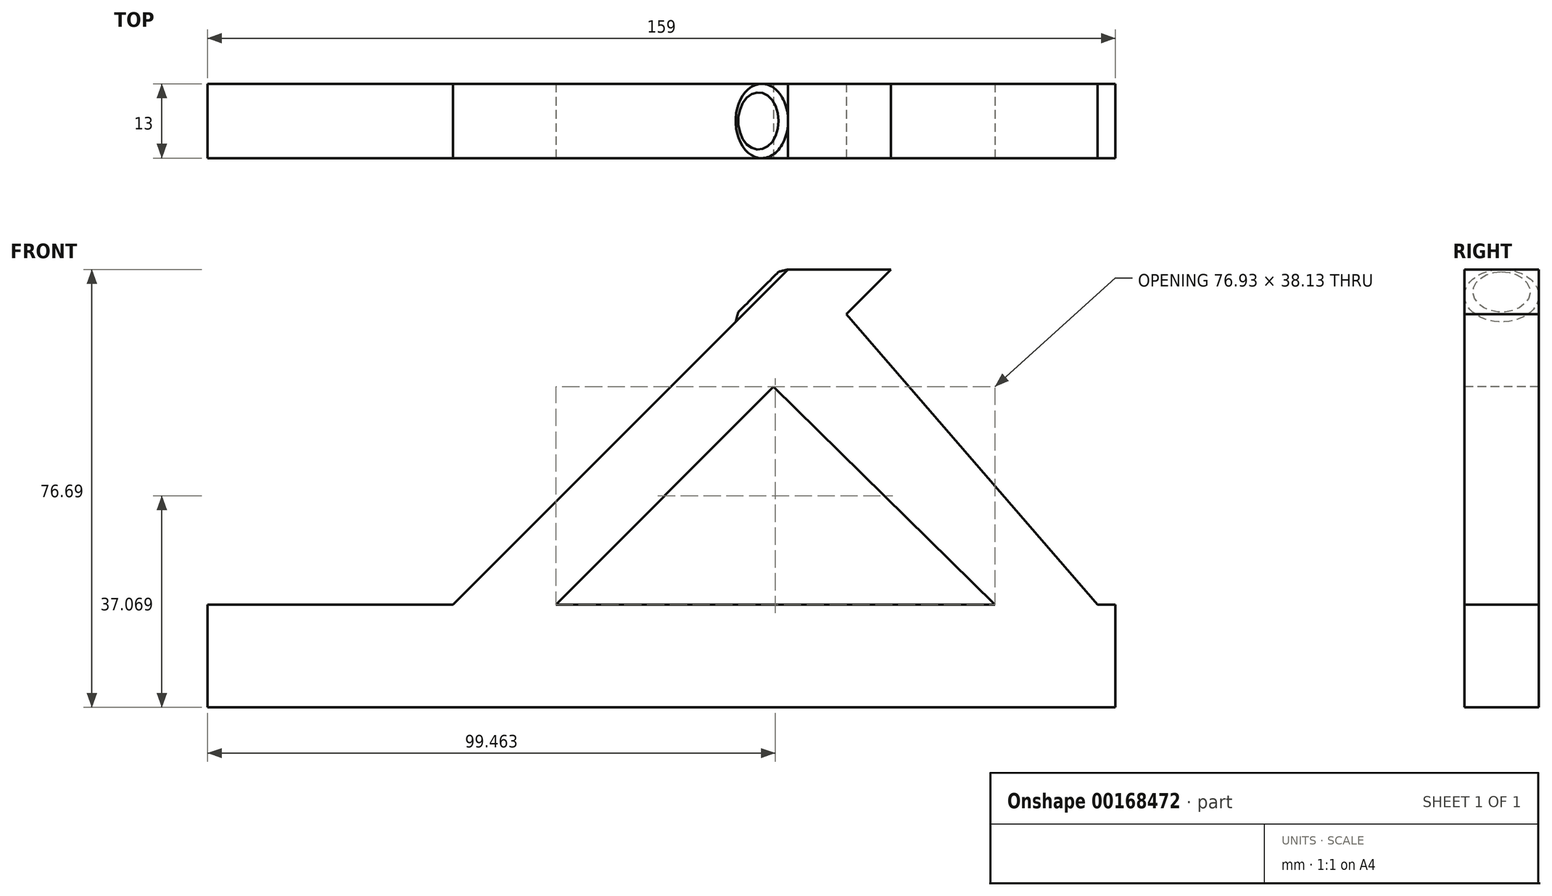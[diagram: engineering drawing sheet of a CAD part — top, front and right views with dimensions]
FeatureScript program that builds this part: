
annotation { "Feature Type Name" : "Feature", "Feature Type Description" : "" }
export const myFeature = defineFeature(function(context is Context, id is Id, definition is map)
    precondition{}
    {
        {
            var Q0;
            Q0=qCreatedBy(makeId("Right.planeOp"),FACE);
            var sketch = newSketch(context, id + "F0", { "sketchPlane" : qUnion([Q0])});
            skLineSegment(sketch, "E0.bottom", {"start": v(50, 50) * mm, "end": v(-50, 50) * mm});
            skLineSegment(sketch, "E0.top", {"start": v(50, -50) * mm, "end": v(-50, -50) * mm});
            skLineSegment(sketch, "E0.left", {"start": v(50, 50) * mm, "end": v(50, -50) * mm});
            skLineSegment(sketch, "E0.right", {"start": v(-50, 50) * mm, "end": v(-50, -50) * mm});
            skPoint(sketch, "E0.middle", {"position": v(0, 0) * mm});
            skLineSegment(sketch, "E1.bottom", {"start": v(6.5, -18.26) * mm, "end": v(-6.5, -18.26) * mm});
            skLineSegment(sketch, "E1.top", {"start": v(6.5, -36.26) * mm, "end": v(-6.5, -36.26) * mm});
            skLineSegment(sketch, "E1.left", {"start": v(6.5, -18.26) * mm, "end": v(6.5, -36.26) * mm});
            skLineSegment(sketch, "E1.right", {"start": v(-6.5, -18.26) * mm, "end": v(-6.5, -36.26) * mm});
            skPoint(sketch, "E1.middle", {"position": v(0, -27.26) * mm});
            skSolve(sketch);
        }
        {
            var Q0;
            Q0=qCreatedBy(makeId("Right.planeOp"),FACE);
            cPlane(context, id + "F1", {"entities" : qUnion([Q0]), "cplaneType" : CPlaneType.OFFSET, "offset" : 96.5 * mm, "width" : 150 * mm, "height" : 150 * mm});
        }
        {
            var Q0;
            Q0=qCreatedBy(id+"F1.planeOp",FACE);
            var sketch = newSketch(context, id + "F2", { "sketchPlane" : qUnion([Q0])});
            skLineSegment(sketch, "E2", {"start": v(-73.65, 36.5) * mm, "end": v(73.12, 36.5) * mm});
            skSolve(sketch);
        }
        {
            var Q0;
            Q0=sQuery(id+"F2.wireOp",EDGE,"E2");
            cPlane(context, id + "F3", {"entities" : qUnion([Q0]), "cplaneType" : CPlaneType.LINE_ANGLE, "offset" : 25 * mm, "angle" : 315 * degree, "width" : 150 * mm, "height" : 150 * mm});
        }
        {
            var Q0;
            Q0=qCreatedBy(id+"F3.planeOp",FACE);
            var sketch = newSketch(context, id + "F4", { "sketchPlane" : qUnion([Q0])});
            skCircle(sketch, "E3", {"center": v(0, 94.05) * mm, "radius": 5 * mm});
            skSolve(sketch);
        }
        {
            var Q0;
            Q0=makeQuery(id+"F0.imprint","IMPRINT",FACE,{"disambiguationData":[TD([[makeQuery(id+"F0.imprint","IMPRINT",EDGE,{"derivedFrom":sQuery(id+"F0.wireOp",EDGE,"E1.bottom")}),1.0]])]});
            extrude(context, id + "F5", {"entities" : qUnion([Q0]), "depth" : 159 * mm});
        }
        {
            var Q0;
            Q0=makeQuery(id+"F5.opExtrude","SWEPT_FACE",FACE,{"disambiguationData":[OSD([sQuery(id+"F0.wireOp",EDGE,"E1.bottom")])]});
            var sketch = newSketch(context, id + "F6", { "sketchPlane" : qUnion([Q0])});
            skLineSegment(sketch, "E4.bottom", {"start": v(61, 6.5) * mm, "end": v(43, 6.5) * mm});
            skLineSegment(sketch, "E4.top", {"start": v(61, -6.5) * mm, "end": v(43, -6.5) * mm});
            skLineSegment(sketch, "E4.left", {"start": v(61, 6.5) * mm, "end": v(61, -6.5) * mm});
            skLineSegment(sketch, "E4.right", {"start": v(43, 6.5) * mm, "end": v(43, -6.5) * mm});
            skPoint(sketch, "E4.middle", {"position": v(52, 0) * mm});
            skSolve(sketch);
        }
        {
            var Q0;
            Q0=qCreatedBy(makeId("Front.planeOp"),FACE);
            var sketch = newSketch(context, id + "F7", { "sketchPlane" : qUnion([Q0])});
            skLineSegment(sketch, "E5", {"start": v(52, -18.26) * mm, "end": v(110.69, 40.43) * mm});
            skSolve(sketch);
        }
        {
            var Q0;
            Q0=makeQuery(id+"F6.imprint","IMPRINT",FACE,{"disambiguationData":[TD([[makeQuery(id+"F6.imprint","IMPRINT",EDGE,{"derivedFrom":sQuery(id+"F6.wireOp",EDGE,"E4.bottom")}),1.0]])]});
            var Q1;
            Q1=sQuery(id+"F7.wireOp",EDGE,"E5");
            sweep(context, id + "F8", {"operationType" : NewBodyOperationType.ADD, "profiles" : qUnion([Q0]), "path" : qUnion([Q1])});
        }
        {
            var Q0;
            Q0=makeQuery(id+"F8.opSweep","SWEPT_FACE",FACE,{"disambiguationData":[OSD([sQuery(id+"F6.wireOp",EDGE,"E4.right"),sQuery(id+"F7.wireOp",EDGE,"E5")])]});
            var sketch = newSketch(context, id + "F9", { "sketchPlane" : qUnion([Q0])});
            skCircle(sketch, "E6", {"center": v(0, 94) * mm, "radius": 6.5 * mm});
            skSolve(sketch);
        }
        {
            var Q1;
            Q1=makeQuery(id+"F4.imprint","IMPRINT",FACE,{"disambiguationData":[TD([[makeQuery(id+"F4.imprint","IMPRINT",EDGE,{"derivedFrom":sQuery(id+"F4.wireOp",EDGE,"E3")}),1.0]])]});
            var Q2;
            {var subQ0=sQuery(id+"F9.wireOp",EDGE,"E6");var subQ1=sQuery(id+"F6.wireOp",EDGE,"E4.right");var subQ2=makeQuery(id+"F9.imprint","INTERSECT",VERTEX,{"derivedFrom":[makeQuery(id+"F8.opSweep","CAP_EDGE",EDGE,{"disambiguationData":[OSD([subQ1,sQuery(id+"F7.wireOp",VERTEX,"E5.end")])],"isStart":false}),subQ0]});Q2=makeQuery(id+"F9.imprint","IMPRINT",FACE,{"disambiguationData":[TD([[makeQuery(id+"F9.imprint","IMPRINT",EDGE,{"disambiguationData":[TD([[subQ2,1.0]])],"derivedFrom":subQ0}),1.0]])]});}
            loft(context, id + "F10", {"operationType" : NewBodyOperationType.ADD, "sheetProfilesArray" : [{ "sheetProfileEntities" : qUnion([Q1]) }, { "sheetProfileEntities" : qUnion([Q2]) }]});
        }
        {
            var Q0;
            Q0=makeQuery(id+"F5.opExtrude","SWEPT_FACE",FACE,{"disambiguationData":[OSD([sQuery(id+"F0.wireOp",EDGE,"E1.bottom")])]});
            var sketch = newSketch(context, id + "F11", { "sketchPlane" : qUnion([Q0])});
            skLineSegment(sketch, "E7.bottom", {"start": v(155.93, 6.5) * mm, "end": v(137.93, 6.5) * mm});
            skLineSegment(sketch, "E7.top", {"start": v(155.93, -6.5) * mm, "end": v(137.93, -6.5) * mm});
            skLineSegment(sketch, "E7.left", {"start": v(155.93, 6.5) * mm, "end": v(155.93, -6.5) * mm});
            skLineSegment(sketch, "E7.right", {"start": v(137.93, 6.5) * mm, "end": v(137.93, -6.5) * mm});
            skPoint(sketch, "E7.middle", {"position": v(146.93, 0) * mm});
            skSolve(sketch);
        }
        {
            var Q0;
            Q0=makeQuery(id+"F8.opSweep","SWEPT_FACE",FACE,{"disambiguationData":[OSD([sQuery(id+"F6.wireOp",EDGE,"E4.left"),sQuery(id+"F7.wireOp",EDGE,"E5")])]});
            var sketch = newSketch(context, id + "F12", { "sketchPlane" : qUnion([Q0])});
            skLineSegment(sketch, "E8.bottom", {"start": v(6.5, 102.15) * mm, "end": v(-6.5, 102.15) * mm});
            skLineSegment(sketch, "E8.top", {"start": v(6.5, 84.15) * mm, "end": v(-6.5, 84.15) * mm});
            skLineSegment(sketch, "E8.left", {"start": v(6.5, 102.15) * mm, "end": v(6.5, 84.15) * mm});
            skLineSegment(sketch, "E8.right", {"start": v(-6.5, 102.15) * mm, "end": v(-6.5, 84.15) * mm});
            skPoint(sketch, "E8.middle", {"position": v(0, 93.15) * mm});
            skSolve(sketch);
        }
        {
            var Q1;
            Q1=makeQuery(id+"F11.imprint","IMPRINT",FACE,{"disambiguationData":[TD([[makeQuery(id+"F11.imprint","IMPRINT",EDGE,{"derivedFrom":sQuery(id+"F11.wireOp",EDGE,"E7.bottom")}),1.0]])]});
            var Q2;
            Q2=makeQuery(id+"F12.imprint","IMPRINT",FACE,{"disambiguationData":[TD([[makeQuery(id+"F12.imprint","IMPRINT",EDGE,{"derivedFrom":sQuery(id+"F12.wireOp",EDGE,"E8.bottom")}),1.0]])]});
            loft(context, id + "F13", {"operationType" : NewBodyOperationType.ADD, "sheetProfilesArray" : [{ "sheetProfileEntities" : qUnion([Q1]) }, { "sheetProfileEntities" : qUnion([Q2]) }]});
        }
    });
